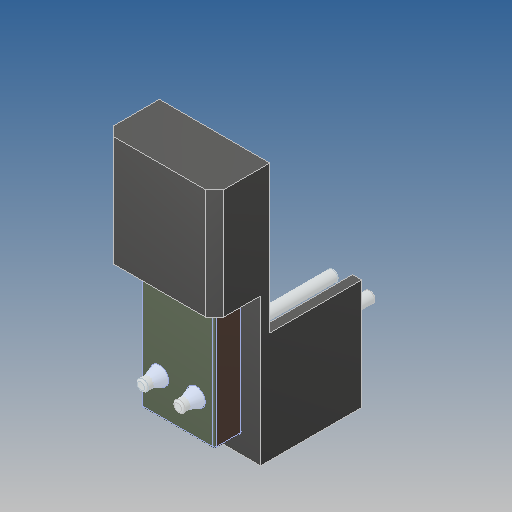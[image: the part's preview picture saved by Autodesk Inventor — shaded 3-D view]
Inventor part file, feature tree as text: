
AUTODESK INVENTOR PART (.ipt)
format: ipt  version: 2020 (Build 240168000, 168)  size: 179,200 bytes
history: mixed  units: mm
features: other x10, fillet x3, chamfer x1, imported_body x1
ambient origin geometry x8: Origin, YZ Plane, XZ Plane, XY Plane, X Axis, Y Axis, Z Axis, Center Point
bodies: Body1 (imported_parasolid), Body2 (imported_parasolid), Body3 (imported_parasolid), Body4 (imported_parasolid), Body5 (imported_parasolid), Body6 (imported_parasolid), Body7 (imported_parasolid)
feature tree (15):
  other  "Твердое тело1"
  other  "Твердое тело2"
  other  "Твердое тело3"
  other  "Твердое тело4"
  other  "Твердое тело5"
  other  "Твердое тело6"
  other  "Твердое тело7"
  chamfer  "Chamfer1"  [1 undecoded]
  other  "Dome1"
  fillet  "Fillet2"  [1 undecoded]
  fillet  "Fillet4"  [1 undecoded]
  fillet  "Fillet5"  [1 undecoded]
  other  "Boss-Extrude9[1]"
  other  "Boss-Extrude9[2]"
  imported_body  NMx_Import_Brep_tag  [imported B-rep: ~60 faces, bbox_mm=[6.0, 14.0, 10.5]]
note: 4 required parameter values undecoded (feature->parameter linkage not recoverable at this tier; creation-order binding heuristic only, values carry confidence <= 0.55)
